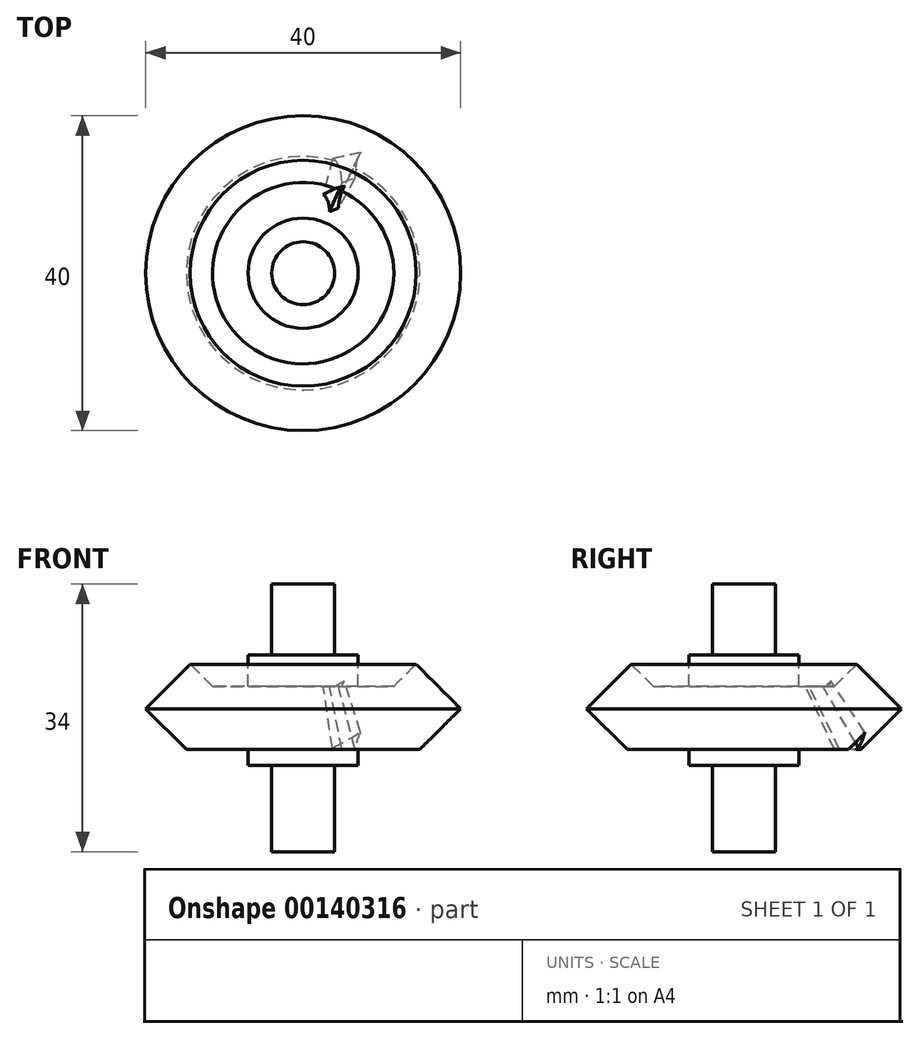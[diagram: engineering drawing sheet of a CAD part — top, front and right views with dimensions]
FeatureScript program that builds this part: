
annotation { "Feature Type Name" : "Feature", "Feature Type Description" : "" }
export const myFeature = defineFeature(function(context is Context, id is Id, definition is map)
    precondition{}
    {
        {
            var Q0;
            Q0=qCreatedBy(makeId("Front.planeOp"),FACE);
            var sketch = newSketch(context, id + "F0", { "sketchPlane" : qUnion([Q0])});
            skLineSegment(sketch, "E0", {"start": v(0, 50) * mm, "end": v(0, -50) * mm, "construction": true});
            skSolve(sketch);
        }
        {
            var Q0;
            Q0=qCreatedBy(makeId("Front.planeOp"),FACE);
            var sketch = newSketch(context, id + "F1", { "sketchPlane" : qUnion([Q0])});
            skLineSegment(sketch, "E1", {"start": v(0, 0) * mm, "end": v(0, 8) * mm});
            skLineSegment(sketch, "E2", {"start": v(0, 8) * mm, "end": v(11.51, 8) * mm});
            skLineSegment(sketch, "E3", {"start": v(14.83, 0) * mm, "end": v(0, 0) * mm});
            skLineSegment(sketch, "E4", {"start": v(11.51, 8) * mm, "end": v(14.34, 10.83) * mm});
            skLineSegment(sketch, "E5", {"start": v(14.34, 10.83) * mm, "end": v(20, 5.17) * mm});
            skLineSegment(sketch, "E6", {"start": v(20, 5.17) * mm, "end": v(14.83, 0) * mm});
            skSolve(sketch);
        }
        {
            var Q0;
            Q0=makeQuery(id+"F1.imprint","IMPRINT",FACE,{"disambiguationData":[TD([[makeQuery(id+"F1.imprint","IMPRINT",EDGE,{"derivedFrom":sQuery(id+"F1.wireOp",EDGE,"E1")}),-1.0]])]});
            var Q1;
            Q1=sQuery(id+"F0.wireOp",EDGE,"E0");
            revolve(context, id + "F2", {"entities" : qUnion([Q0]), "axis" : qUnion([Q1]), "revolveType" : RevolveType.FULL});
        }
        {
            var Q0;
            Q0=sQuery(id+"F1.wireOp",EDGE,"E5");
            var Q1;
            Q1=sQuery(id+"F1.wireOp",VERTEX,"E6.start");
            cPlane(context, id + "F3", {"entities" : qUnion([Q0, Q1]), "cplaneType" : CPlaneType.LINE_POINT, "offset" : 25 * mm, "width" : 150 * mm, "height" : 150 * mm});
        }
        {
            var Q0;
            Q0=qCreatedBy(id+"F3.planeOp",FACE);
            var sketch = newSketch(context, id + "F4", { "sketchPlane" : qUnion([Q0])});
            skLineSegment(sketch, "E7", {"start": v(15.3, 1.25) * mm, "end": v(15.3, -1.25) * mm});
            skLineSegment(sketch, "E8", {"start": v(20.3, -3.16) * mm, "end": v(20.3, 3.16) * mm});
            skLineSegment(sketch, "E9", {"start": v(14.27, 0) * mm, "end": v(19.27, 0) * mm, "construction": true});
            skArc(sketch, "E10", {"start": v(20.3, -3.16) * mm, "mid": v(17.98, -1.74) * mm, "end": v(15.3, -1.25) * mm});
            skArc(sketch, "E11.MirrorCS", {"start": v(20.3, 3.16) * mm, "mid": v(17.98, 1.74) * mm, "end": v(15.3, 1.25) * mm});
            skSolve(sketch);
        }
        {
            var Q0;
            Q0=qCreatedBy(makeId("Front.planeOp"),FACE);
            var sketch = newSketch(context, id + "F5", { "sketchPlane" : qUnion([Q0])});
            skLineSegment(sketch, "E12", {"start": v(0, 25.17) * mm, "end": v(75.17, -50) * mm, "construction": true});
            skSolve(sketch);
        }
        {
            var Q1;
            Q1=makeQuery(id+"F4.imprint","IMPRINT",FACE,{"disambiguationData":[TD([[makeQuery(id+"F4.imprint","IMPRINT",EDGE,{"derivedFrom":sQuery(id+"F4.wireOp",EDGE,"E7")}),1.0]])]});
            var Q2;
            Q2=sQuery(id+"F5.wireOp",VERTEX,"E12.start");
            loft(context, id + "F6", {"operationType" : NewBodyOperationType.REMOVE, "sheetProfilesArray" : [{ "sheetProfileEntities" : qUnion([Q1]) }, { "sheetProfileEntities" : qUnion([Q2]) }]});
        }
        {
            var Q0;
            Q0=qCreatedBy(makeId("Front.planeOp"),FACE);
            var sketch = newSketch(context, id + "F7", { "sketchPlane" : qUnion([Q0])});
            skLineSegment(sketch, "E13.bottom", {"start": v(4, 12) * mm, "end": v(7, 12) * mm});
            skLineSegment(sketch, "E13.top", {"start": v(4, -2) * mm, "end": v(7, -2) * mm});
            skLineSegment(sketch, "E13.right", {"start": v(7, 12) * mm, "end": v(7, -2) * mm});
            skLineSegment(sketch, "E14.bottom", {"start": v(0, 21) * mm, "end": v(4, 21) * mm});
            skLineSegment(sketch, "E14.top", {"start": v(0, -13) * mm, "end": v(4, -13) * mm});
            skLineSegment(sketch, "E14.left", {"start": v(0, 21) * mm, "end": v(0, -13) * mm});
            skLineSegment(sketch, "E14.right", {"start": v(4, 21) * mm, "end": v(4, 12) * mm});
            skLineSegment(sketch, "E15.trimOffspring", {"start": v(4, -2) * mm, "end": v(4, -13) * mm});
            skSolve(sketch);
        }
        {
            var Q0;
            Q0=makeQuery(id+"F7.imprint","IMPRINT",FACE,{"disambiguationData":[TD([[makeQuery(id+"F7.imprint","IMPRINT",EDGE,{"derivedFrom":sQuery(id+"F7.wireOp",EDGE,"E13.bottom")}),-1.0]])]});
            var Q1;
            Q1=sQuery(id+"F0.wireOp",EDGE,"E0");
            revolve(context, id + "F8", {"operationType" : NewBodyOperationType.ADD, "entities" : qUnion([Q0]), "axis" : qUnion([Q1]), "revolveType" : RevolveType.FULL});
        }
    });
